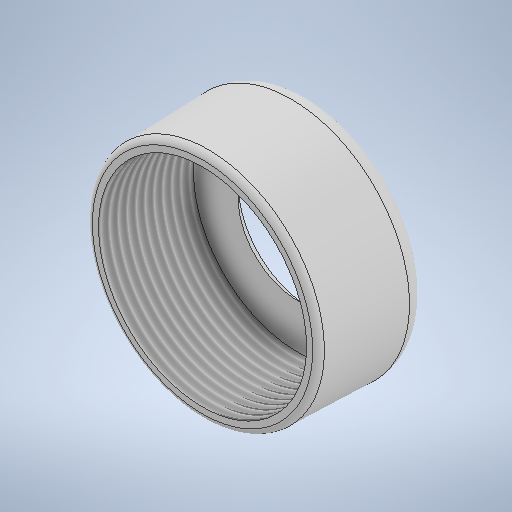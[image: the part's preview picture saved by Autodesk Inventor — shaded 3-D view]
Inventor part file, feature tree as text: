
AUTODESK INVENTOR PART (.ipt)
format: ipt  version: 2025.1 (Build 291241000, 241)  size: 320,000 bytes
history: native  units: mm
features: fillet x2, revolve x1, chamfer x1, thread x1, sketch x1
ambient origin geometry x8: Origin, YZ Plane, XZ Plane, XY Plane, X Axis, Y Axis, Z Axis, Center Point
bodies: Volumenkörper1 (feature_tree)
feature tree (6):
  revolve  "Umdrehung1"
  chamfer  "Fasen1"  Distance=16.0mm
  thread  "Gewinde1"  [1 undecoded]
  fillet  "Rundung1"  Radius=2.0mm
  fillet  "Rundung2"  [1 undecoded]
  sketch  "Skizze1"  dims[d0=35.0mm d1=16.0mm d2=20.0mm d4=2.0mm d5=90.0deg d6=2.0mm d7=2.0mm d8=45.0deg d9=10.0mm d10=2.0mm d11=16.0mm d12=0.0mm d13=3.0mm d14=1.0mm]
note: 2 required parameter values undecoded (feature->parameter linkage not recoverable at this tier; creation-order binding heuristic only, values carry confidence <= 0.55)
